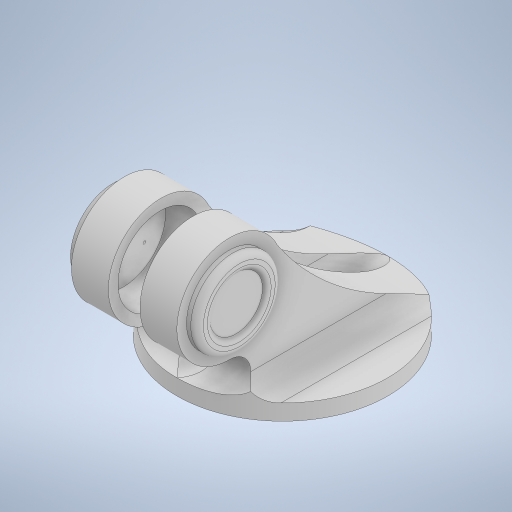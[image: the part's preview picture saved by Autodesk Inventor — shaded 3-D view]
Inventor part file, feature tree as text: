
AUTODESK INVENTOR PART (.ipt)
format: ipt  version: 2024 (Build 280153000, 153)  size: 423,424 bytes
history: native  units: mm
features: extrude x11, sketch x9, fillet x3, mirror x3
ambient origin geometry x8: Origin, YZ Plane, XZ Plane, XY Plane, X Axis, Y Axis, Z Axis, Center Point
bodies: Solid1 (feature_tree)
feature tree (26):
  sketch  "Sketch1"  dims[d0=166.0mm d1=200.0mm]
  extrude  "Extrusion1"  Depth=200.0mm
  extrude  "Extrusion2"  Depth=10.0mm TaperAngle=0.0deg
  extrude  "Extrusion3"  Depth=40.0mm
  extrude  "Extrusion4"  Depth=50.0mm
  extrude  "Extrusion5"  Depth=50.0mm TaperAngle=0.0deg
  sketch  "Sketch5"  dims[d22=20.0mm d23=50.0mm d24=0.0mm]
  extrude  "Extrusion6"  Depth=20.0mm
  extrude  "Extrusion7"  Depth=50.0mm TaperAngle=0.0deg
  fillet  "Fillet3"  Radius=50.0mm
  extrude  "Extrusion8"  Depth=7.0mm TaperAngle=0.0deg
  extrude  "Extrusion9"  Depth=15.0mm
  mirror  "Mirror1"
  extrude  "Extrusion10"  TaperAngle=0.0deg  [1 undecoded]
  mirror  "Mirror2"
  extrude  "Extrusion11"  Depth=15.0mm
  fillet  "Fillet4"  Radius=2.5mm
  fillet  "Fillet5"  Radius=5.0mm
  mirror  "Mirror3"
  sketch  "Sketch2"  dims[d2=15.0mm d3=0.0mm d4=10.0mm d5=0.0mm]
  sketch  "Sketch3"  dims[d15=40.0mm d19=100.0mm]
  sketch  "Sketch4"  dims[d20=50.0mm d21=50.0mm]
  sketch  "Sketch6"  dims[d25=20.0mm d26=0.0mm d29=80.0mm]
  sketch  "Sketch7"  dims[d30=0.0mm d31=45.0mm d32=0.0mm d33=50.0mm]
  sketch  "Sketch8"  dims[d34=10.0mm d35=0.0mm d36=7.0mm d37=0.0mm]
  sketch  "Sketch9"  dims[d38=6.0mm d40=2.5mm d41=0.0mm d42=6.0mm d44=2.5mm d45=5.0mm d46=0.0mm d48=20.0mm d49=20.0mm d50=90.0mm d51=45.0mm d52=0.0mm d53=15.0mm d54=300.0mm d55=0.0mm d56=250.0mm d57=200.0mm d58=20.0mm d59=0.0mm d60=20.0mm d61=15.0mm]
note: 1 required parameter value undecoded (feature->parameter linkage not recoverable at this tier; creation-order binding heuristic only, values carry confidence <= 0.55)
